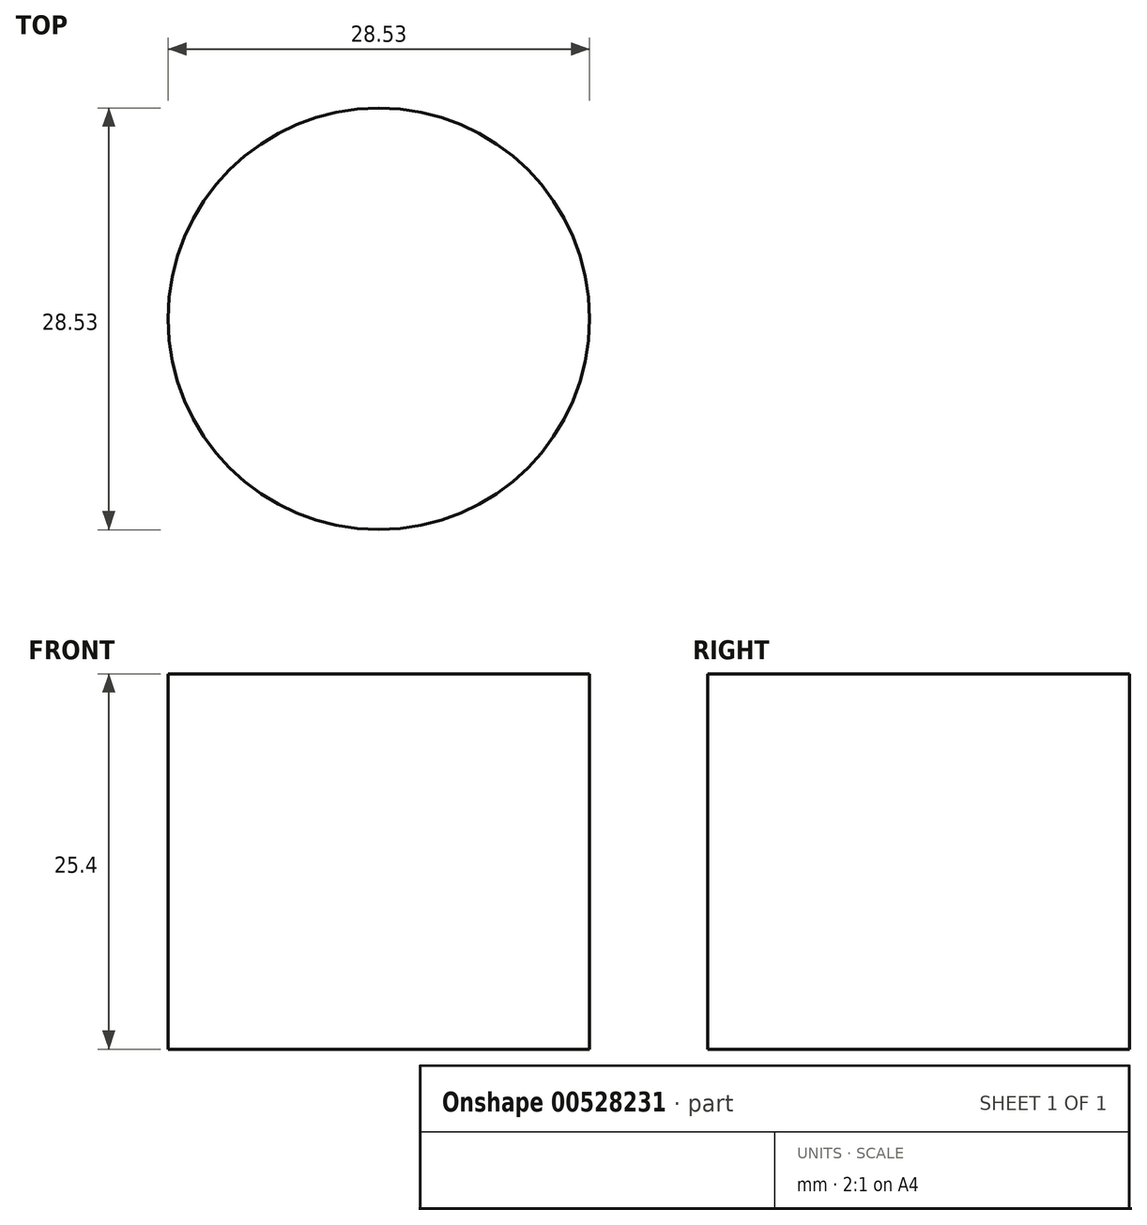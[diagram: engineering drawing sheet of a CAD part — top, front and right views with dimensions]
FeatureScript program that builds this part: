
annotation { "Feature Type Name" : "Feature", "Feature Type Description" : "" }
export const myFeature = defineFeature(function(context is Context, id is Id, definition is map)
    precondition{}
    {
        {
            var Q0;
            Q0=qCreatedBy(makeId("Top.planeOp"),FACE);
            var sketch = newSketch(context, id + "F0", { "sketchPlane" : qUnion([Q0])});
            skCircle(sketch, "E0", {"center": v(-97.09, 19.2) * mm, "radius": 14.26 * mm});
            skSolve(sketch);
        }
        {
            var Q0;
            Q0 = qSketchRegion(id + "F0", true);
            extrude(context, id + "F1", {"entities" : qUnion([Q0]), "depth" : 25.4 * mm, "offsetDistance" : 25.4 * mm});
        }
    });
